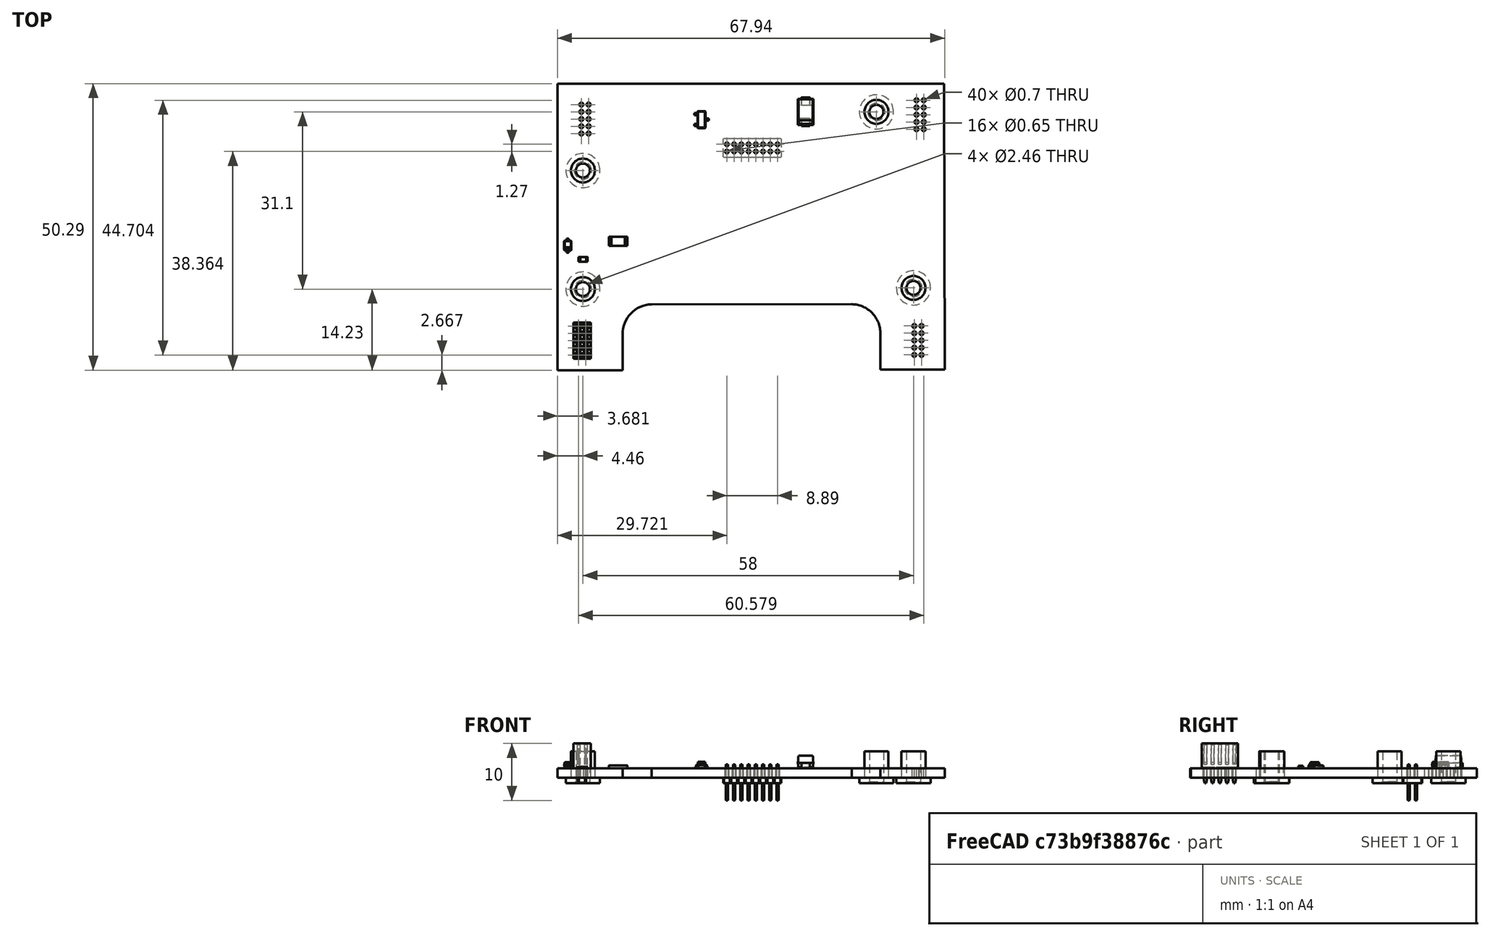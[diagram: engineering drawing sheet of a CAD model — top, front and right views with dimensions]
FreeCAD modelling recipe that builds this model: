
FCSTD DOCUMENT  (FreeCAD 1.0R39109 (Git))
Label: DICAddonBoard
License: All rights reserved
LicenseURL: http://en.wikipedia.org/wiki/All_rights_reserved
objects: App::Link×70, Part::Feature×18, App::Part×5, PartDesign::CoordinateSystem×1, Sketcher::SketchObject×1
note: 21 computed .brp shape members not serialized (recipe doc carries the construction recipe); baked Part::Feature solids carry a one-line shape summary decoded from their .brp

FEATURE [PartDesign::CoordinateSystem] Local_CS_25db
  AttacherType = Attacher::AttachEngine3D
  MapMode = 2
FEATURE [Part::Feature] Pcb_25db
  shape: bbox 67.95 x 50.29 x 1.6 mm, 68 faces (baked)
FEATURE [Sketcher::SketchObject] PCB_Sketch_25db
  ArcFitTolerance = 1e-06
  FullyConstrained = false
  MakeInternals = false
  sketch-geometry (10):
    g0: LineSegment StartX=11.938 StartY=-11.938 StartZ=0 EndX=11.938 EndY=-62.23 EndZ=0
    g1: LineSegment StartX=68.58 StartY=-62.103 StartZ=0 EndX=79.883 EndY=-62.103 EndZ=0
    g2: LineSegment StartX=11.938 StartY=-62.23 StartZ=0 EndX=23.3806 EndY=-62.23 EndZ=0
    g3: LineSegment StartX=23.3806 StartY=-62.23 StartZ=0 EndX=23.368 EndY=-55.9897 EndZ=0
    g4: LineSegment StartX=79.756 StartY=-11.938 StartZ=0 EndX=11.938 EndY=-11.938 EndZ=0
    g5: LineSegment StartX=68.5926 StartY=-55.8627 StartZ=0 EndX=68.58 EndY=-62.103 EndZ=0
    g6: LineSegment StartX=28.448 StartY=-50.673 StartZ=0 EndX=63.5588 EndY=-50.6595 EndZ=0
    g7: LineSegment StartX=79.883 StartY=-62.103 StartZ=0 EndX=79.756 EndY=-11.938 EndZ=0
    g8: ArcOfCircle CenterX=28.5729 CenterY=-55.8776 CenterZ=0 NormalX=0 NormalY=0 NormalZ=-1 AngleXU=-0.0215457 Radius=5.20607 StartAngle=0 EndAngle=1.56835
    g9: ArcOfCircle CenterX=63.5 CenterY=-55.753 CenterZ=0 NormalX=0 NormalY=0 NormalZ=-1 AngleXU=1.58235 Radius=5.09379 StartAngle=-4.7832e-11 EndAngle=1.58079
  constraints (10):
    c: Coincident(g0,g2)
    c: Coincident(g0,g4)
    c: Coincident(g3,g8)
    c: Coincident(g2,g3)
    c: Coincident(g6,g8)
    c: Coincident(g6,g9)
    c: Coincident(g1,g5)
    c: Coincident(g5,g9)
    c: Coincident(g4,g7)
    c: Coincident(g1,g7)
FEATURE [Part::Feature] Shape  label="Q6_SOT_23_ffd5320711a5"
  Placement = pos=(37.211,-18.262,0) rot=(0,0,1;0rad)
  shape: bbox 2.5 x 3 x 1.2 mm, 76 faces (baked)
FEATURE [Part::Feature] Shape001  label="D16_D_SOD_323_d7651d96f6c3"
  Placement = pos=(13.7425,-40.366,0) rot=(0,0,1;1.5708rad)
  shape: bbox 1.25 x 2.5 x 1.1 mm, 67 faces (baked)
FEATURE [Part::Feature] Shape002  label="J6_PinSocket_2x05_P127mm_Vertical_83ee9fbb584e"
  Placement = pos=(16.891,-54.483,0) rot=(0,0,1;0rad)
  shape: bbox 3.05 x 6.35 x 7 mm, 320 faces (baked)
FEATURE [Part::Feature] Shape003  label="R41_R_0603_1608Metric_127fa2614279"
  Placement = pos=(16.433,-42.799,0) rot=(0,0,1;0rad)
  shape: bbox 1.6 x 0.8 x 0.45 mm, 26 faces (baked)
FEATURE [App::Link] R41_R_0603_1608Metric_127fa2614279_ln_  label="R12_R_0603_1608Metric_a0e0216bc4ce"
  LinkPlacement = pos=(29.9212,-15.0876,0) rot=(0,0,1;3.14159rad)
  LinkedObject = -> Shape003
  Placement = pos=(29.9212,-15.0876,0) rot=(0,0,1;3.14159rad)
FEATURE [App::Link] R41_R_0603_1608Metric_127fa2614279_ln_001  label="R13_R_0603_1608Metric_473b31106c1b"
  LinkPlacement = pos=(32.639,-18.77,0) rot=(0,0,1;1.5708rad)
  LinkedObject = -> Shape003
  Placement = pos=(32.639,-18.77,0) rot=(0,0,1;1.5708rad)
FEATURE [Part::Feature] Shape004  label="D6_D_SMA_735d77270f2b"
  Placement = pos=(55.477,-16.896,0) rot=(0,0,1;1.5708rad)
  shape: bbox 2.7 x 5 x 2.22 mm, 41 faces (baked)
FEATURE [App::Link] R41_R_0603_1608Metric_127fa2614279_ln_002  label="R9_R_0603_1608Metric_79f8a3dd54a6"
  LinkPlacement = pos=(61.214,-13.9059,0) rot=(0,0,1;3.14159rad)
  LinkedObject = -> Shape003
  Placement = pos=(61.214,-13.9059,0) rot=(0,0,1;3.14159rad)
FEATURE [App::Link] R41_R_0603_1608Metric_127fa2614279_ln_003  label="R31_R_0603_1608Metric_c49473b8d088"
  LinkPlacement = pos=(50.473,-46.8085,0) rot=(0,0,1;1.5708rad)
  LinkedObject = -> Shape003
  Placement = pos=(50.473,-46.8085,0) rot=(0,0,1;1.5708rad)
FEATURE [App::Link] R41_R_0603_1608Metric_127fa2614279_ln_004  label="R14_R_0603_1608Metric_d7197a96d642"
  LinkPlacement = pos=(37.41,-15.722,0) rot=(0,0,1;0rad)
  LinkedObject = -> Shape003
  Placement = pos=(37.41,-15.722,0) rot=(0,0,1;0rad)
FEATURE [App::Link] R41_R_0603_1608Metric_127fa2614279_ln_005  label="R35_R_0603_1608Metric_1226fcb64f1c"
  LinkPlacement = pos=(47.933,-37.9245,0) rot=(0,0,1;0rad)
  LinkedObject = -> Shape003
  Placement = pos=(47.933,-37.9245,0) rot=(0,0,1;0rad)
FEATURE [App::Link] D6_D_SMA_735d77270f2b_ln_  label="D17_D_SMA_0876cbf78d6f"
  LinkPlacement = pos=(20.828,-34.925,0) rot=(0,0,1;1.5708rad)
  LinkedObject = -> Shape004
  Placement = pos=(20.828,-34.925,0) rot=(0,0,1;1.5708rad)
FEATURE [App::Link] D6_D_SMA_735d77270f2b_ln_001  label="D15_D_SMA_1207fe425828"
  LinkPlacement = pos=(53.255,-43.21,0) rot=(0,0,1;0rad)
  LinkedObject = -> Shape004
  Placement = pos=(53.255,-43.21,0) rot=(0,0,1;0rad)
FEATURE [App::Link] D16_D_SOD_323_d7651d96f6c3_ln_  label="D13_D_SOD_323_07ad6b2cef4e"
  LinkPlacement = pos=(47.826,-32.3365,0) rot=(0,0,1;3.14159rad)
  LinkedObject = -> Shape001
  Placement = pos=(47.826,-32.3365,0) rot=(0,0,1;3.14159rad)
FEATURE [App::Link] R41_R_0603_1608Metric_127fa2614279_ln_006  label="R32_R_0603_1608Metric_48fbb2cf6ecc"
  LinkPlacement = pos=(56.061,-46.705,0) rot=(0,0,1;1.5708rad)
  LinkedObject = -> Shape003
  Placement = pos=(56.061,-46.705,0) rot=(0,0,1;1.5708rad)
FEATURE [App::Link] R41_R_0603_1608Metric_127fa2614279_ln_007  label="R24_R_0603_1608Metric_9565dda51c7b"
  LinkPlacement = pos=(50.461,-36.098,0) rot=(0,0,1;1.5708rad)
  LinkedObject = -> Shape003
  Placement = pos=(50.461,-36.098,0) rot=(0,0,1;1.5708rad)
FEATURE [App::Link] R41_R_0603_1608Metric_127fa2614279_ln_008  label="R39_R_0603_1608Metric_0d8059b3905e"
  LinkPlacement = pos=(27.857,-32.131,0) rot=(0,0,1;3.14159rad)
  LinkedObject = -> Shape003
  Placement = pos=(27.857,-32.131,0) rot=(0,0,1;3.14159rad)
FEATURE [App::Link] R41_R_0603_1608Metric_127fa2614279_ln_009  label="R11_R_0603_1608Metric_e8feb780e285"
  LinkPlacement = pos=(37.363,-14.198,0) rot=(0,0,1;0rad)
  LinkedObject = -> Shape003
  Placement = pos=(37.363,-14.198,0) rot=(0,0,1;0rad)
FEATURE [App::Link] D6_D_SMA_735d77270f2b_ln_002  label="D9_D_SMA_59bcf57c5f9f"
  LinkPlacement = pos=(51.943,-16.865,0) rot=(0,0,1;1.5708rad)
  LinkedObject = -> Shape004
  Placement = pos=(51.943,-16.865,0) rot=(0,0,1;1.5708rad)
FEATURE [App::Link] D6_D_SMA_735d77270f2b_ln_003  label="D18_D_SMA_56b2f2076145"
  LinkPlacement = pos=(24.362,-34.925,0) rot=(0,0,1;1.5708rad)
  LinkedObject = -> Shape004
  Placement = pos=(24.362,-34.925,0) rot=(0,0,1;1.5708rad)
FEATURE [App::Link] R41_R_0603_1608Metric_127fa2614279_ln_010  label="R37_R_0603_1608Metric_b9a5ae661070"
  LinkPlacement = pos=(17.25,-32.004,0) rot=(0,0,1;0rad)
  LinkedObject = -> Shape003
  Placement = pos=(17.25,-32.004,0) rot=(0,0,1;0rad)
FEATURE [App::Link] R41_R_0603_1608Metric_127fa2614279_ln_011  label="R34_R_0603_1608Metric_5b0c20e38f9c"
  LinkPlacement = pos=(44.504,-34.1145,0) rot=(0,0,1;3.14159rad)
  LinkedObject = -> Shape003
  Placement = pos=(44.504,-34.1145,0) rot=(0,0,1;3.14159rad)
FEATURE [App::Link] R41_R_0603_1608Metric_127fa2614279_ln_012  label="R33_R_0603_1608Metric_6760e7cc6251"
  LinkPlacement = pos=(44.0995,-32.3365,0) rot=(0,0,1;3.14159rad)
  LinkedObject = -> Shape003
  Placement = pos=(44.0995,-32.3365,0) rot=(0,0,1;3.14159rad)
FEATURE [App::Link] D16_D_SOD_323_d7651d96f6c3_ln_001  label="D4_D_SOD_323_fbe22daa305a"
  LinkPlacement = pos=(30.861,-18.2655,0) rot=(0,0,1;1.5708rad)
  LinkedObject = -> Shape001
  Placement = pos=(30.861,-18.2655,0) rot=(0,0,1;1.5708rad)
FEATURE [Part::Feature] Shape005  label="TH6_R_1206_3216Metric_a4174fc2a386"
  Placement = pos=(22.584,-39.624,0) rot=(0,0,1;3.14159rad)
  shape: bbox 3.2 x 1.6 x 0.55 mm, 26 faces (baked)
FEATURE [App::Link] R41_R_0603_1608Metric_127fa2614279_ln_013  label="R40_R_0603_1608Metric_99d0bb74b373"
  LinkPlacement = pos=(13.7425,-36.703,0) rot=(0,0,1;1.5708rad)
  LinkedObject = -> Shape003
  Placement = pos=(13.7425,-36.703,0) rot=(0,0,1;1.5708rad)
FEATURE [App::Link] R41_R_0603_1608Metric_127fa2614279_ln_014  label="R8_R_0603_1608Metric_f9849ceb0926"
  LinkPlacement = pos=(61.087,-19.4939,0) rot=(0,0,1;3.14159rad)
  LinkedObject = -> Shape003
  Placement = pos=(61.087,-19.4939,0) rot=(0,0,1;3.14159rad)
FEATURE [App::Link] R41_R_0603_1608Metric_127fa2614279_ln_015  label="R36_R_0603_1608Metric_b33a5e9c3cf1"
  LinkPlacement = pos=(17.377,-37.592,0) rot=(0,0,1;3.14159rad)
  LinkedObject = -> Shape003
  Placement = pos=(17.377,-37.592,0) rot=(0,0,1;3.14159rad)
FEATURE [App::Link] Q6_SOT_23_ffd5320711a5_ln_  label="Q18_SOT_23_5dae6c215293"
  LinkPlacement = pos=(16.6635,-40.259,0) rot=(0,0,1;3.14159rad)
  LinkedObject = -> Shape
  Placement = pos=(16.6635,-40.259,0) rot=(0,0,1;3.14159rad)
FEATURE [App::Link] J6_PinSocket_2x05_P127mm_Vertical_83ee9fbb584e_ln_  label="J2_PinSocket_2x05_P127mm_Vertical_fade8c78a2a7"
  LinkPlacement = pos=(76.2,-14.859,0) rot=(0,0,1;0rad)
  LinkedObject = -> Shape002
  Placement = pos=(76.2,-14.859,0) rot=(0,0,1;0rad)
FEATURE [App::Link] J6_PinSocket_2x05_P127mm_Vertical_83ee9fbb584e_ln_001  label="J5_PinSocket_2x05_P127mm_Vertical_c59673f5576a"
  LinkPlacement = pos=(16.129,-20.701,0) rot=(0,0,1;3.14159rad)
  LinkedObject = -> Shape002
  Placement = pos=(16.129,-20.701,0) rot=(0,0,1;3.14159rad)
FEATURE [App::Link] TH6_R_1206_3216Metric_a4174fc2a386_ln_  label="TH2_R_1206_3216Metric_52bc38417804"
  LinkPlacement = pos=(41.529,-18.262,0) rot=(0,0,1;1.5708rad)
  LinkedObject = -> Shape005
  Placement = pos=(41.529,-18.262,0) rot=(0,0,1;1.5708rad)
FEATURE [App::Link] D6_D_SMA_735d77270f2b_ln_004  label="D14_D_SMA_40db2f55f09c"
  LinkPlacement = pos=(53.255,-39.584,0) rot=(0,0,1;0rad)
  LinkedObject = -> Shape004
  Placement = pos=(53.255,-39.584,0) rot=(0,0,1;0rad)
FEATURE [App::Link] R41_R_0603_1608Metric_127fa2614279_ln_016  label="R42_R_0603_1608Metric_3962cb7ffa21"
  LinkPlacement = pos=(19.3305,-40.386,0) rot=(0,0,1;1.5708rad)
  LinkedObject = -> Shape003
  Placement = pos=(19.3305,-40.386,0) rot=(0,0,1;1.5708rad)
FEATURE [App::Link] J6_PinSocket_2x05_P127mm_Vertical_83ee9fbb584e_ln_002  label="J4_PinSocket_2x05_P127mm_Vertical_839abc38b667"
  LinkPlacement = pos=(75.819,-54.473,0) rot=(0,0,1;0rad)
  LinkedObject = -> Shape002
  Placement = pos=(75.819,-54.473,0) rot=(0,0,1;0rad)
FEATURE [App::Link] R41_R_0603_1608Metric_127fa2614279_ln_017  label="R10_R_0603_1608Metric_f7e09fcf0586"
  LinkPlacement = pos=(48.387,-13.563,0) rot=(0,0,1;3.14159rad)
  LinkedObject = -> Shape003
  Placement = pos=(48.387,-13.563,0) rot=(0,0,1;3.14159rad)
FEATURE [App::Link] R41_R_0603_1608Metric_127fa2614279_ln_018  label="R38_R_0603_1608Metric_5053fa264887"
  LinkPlacement = pos=(27.984,-37.719,0) rot=(0,0,1;3.14159rad)
  LinkedObject = -> Shape003
  Placement = pos=(27.984,-37.719,0) rot=(0,0,1;3.14159rad)
FEATURE [App::Link] R41_R_0603_1608Metric_127fa2614279_ln_019  label="R30_R_0603_1608Metric_0ef8a02bf31b"
  LinkPlacement = pos=(56.061,-36.0085,0) rot=(0,0,-1;1.5708rad)
  LinkedObject = -> Shape003
  Placement = pos=(56.061,-36.0085,0) rot=(0,0,-1;1.5708rad)
FEATURE [App::Link] Q6_SOT_23_ffd5320711a5_ln_001  label="Q15_SOT_23_f88ca606a138"
  LinkPlacement = pos=(47.933,-35.2575,0) rot=(0,0,1;1.5708rad)
  LinkedObject = -> Shape
  Placement = pos=(47.933,-35.2575,0) rot=(0,0,1;1.5708rad)
FEATURE [App::Link] TH6_R_1206_3216Metric_a4174fc2a386_ln_001  label="TH4_R_1206_3216Metric_6cedd577e318"
  LinkPlacement = pos=(48.568,-41.178,0) rot=(0,0,1;1.5708rad)
  LinkedObject = -> Shape005
  Placement = pos=(48.568,-41.178,0) rot=(0,0,1;1.5708rad)
FEATURE [App::Part] Top_25db
  Group = -> [Shape,Shape001,Shape002,Shape003,R41_R_0603_1608Metric_127fa2614279_ln_,R41_R_0603_1608Metric_127fa2614279_ln_001,Shape004,R41_R_0603_1608Metric_127fa2614279_ln_002,R41_R_0603_1608Metric_127fa2614279_ln_003,R41_R_0603_1608Metric_127fa2614279_ln_004,R41_R_0603_1608Metric_127fa2614279_ln_005,D6_D_SMA_735d77270f2b_ln_,D6_D_SMA_735d77270f2b_ln_001,D16_D_SOD_323_d7651d96f6c3_ln_,+26 more]
  Origin = -> Origin003
FEATURE [App::Link] R41_R_0603_1608Metric_127fa2614279_ln_020  label="R16_R_0603_1608Metric_7932c1e08af1"
  LinkPlacement = pos=(41.275,-42.313,-1.6) rot=(0.707107,0.707107,0;3.14159rad)
  LinkedObject = -> Shape003
  Placement = pos=(41.275,-42.313,-1.6) rot=(0.707107,0.707107,0;3.14159rad)
FEATURE [App::Link] R41_R_0603_1608Metric_127fa2614279_ln_021  label="R25_R_0603_1608Metric_af43064dc6b6"
  LinkPlacement = pos=(74.996,-34.8215,-1.6) rot=(0.707107,-0.707107,0;3.14159rad)
  LinkedObject = -> Shape003
  Placement = pos=(74.996,-34.8215,-1.6) rot=(0.707107,-0.707107,0;3.14159rad)
FEATURE [App::Link] R41_R_0603_1608Metric_127fa2614279_ln_022  label="R3_R_0603_1608Metric_90eb9fac611c"
  LinkPlacement = pos=(27.8525,-37.777,-1.6) rot=(0.707107,0.707107,0;3.14159rad)
  LinkedObject = -> Shape003
  Placement = pos=(27.8525,-37.777,-1.6) rot=(0.707107,0.707107,0;3.14159rad)
FEATURE [App::Link] R41_R_0603_1608Metric_127fa2614279_ln_023  label="R2_R_0603_1608Metric_a95339afed33"
  LinkPlacement = pos=(22.3534,-27.095,-1.6) rot=(0.707107,0.707107,0;3.14159rad)
  LinkedObject = -> Shape003
  Placement = pos=(22.3534,-27.095,-1.6) rot=(0.707107,0.707107,0;3.14159rad)
FEATURE [App::Link] R41_R_0603_1608Metric_127fa2614279_ln_024  label="R29_R_0603_1608Metric_a323e5d2541c"
  LinkPlacement = pos=(69.088,-31.2255,-1.6) rot=(0.707107,-0.707107,0;3.14159rad)
  LinkedObject = -> Shape003
  Placement = pos=(69.088,-31.2255,-1.6) rot=(0.707107,-0.707107,0;3.14159rad)
FEATURE [App::Link] R41_R_0603_1608Metric_127fa2614279_ln_025  label="R1_R_0603_1608Metric_b07fb1c3085f"
  LinkPlacement = pos=(27.9414,-27.222,-1.6) rot=(0.707107,0.707107,0;3.14159rad)
  LinkedObject = -> Shape003
  Placement = pos=(27.9414,-27.222,-1.6) rot=(0.707107,0.707107,0;3.14159rad)
FEATURE [App::Link] R41_R_0603_1608Metric_127fa2614279_ln_026  label="R18_R_0603_1608Metric_5d82281689e8"
  LinkPlacement = pos=(26.7885,-42.672,-1.6) rot=(0,1,0;3.14159rad)
  LinkedObject = -> Shape003
  Placement = pos=(26.7885,-42.672,-1.6) rot=(0,1,0;3.14159rad)
FEATURE [App::Link] R41_R_0603_1608Metric_127fa2614279_ln_027  label="R27_R_0603_1608Metric_214af474eae8"
  LinkPlacement = pos=(75.9085,-41.275,-1.6) rot=(1,0,0;3.14159rad)
  LinkedObject = -> Shape003
  Placement = pos=(75.9085,-41.275,-1.6) rot=(1,0,0;3.14159rad)
FEATURE [App::Link] D6_D_SMA_735d77270f2b_ln_005  label="D11_D_SMA_1ba17688d2f4"
  LinkPlacement = pos=(38.449,-38.735,-1.6) rot=(1,0,0;3.14159rad)
  LinkedObject = -> Shape004
  Placement = pos=(38.449,-38.735,-1.6) rot=(1,0,0;3.14159rad)
FEATURE [App::Link] R41_R_0603_1608Metric_127fa2614279_ln_028  label="R17_R_0603_1608Metric_89ce4ec7833c"
  LinkPlacement = pos=(26.8355,-48.26,-1.6) rot=(1,0,0;3.14159rad)
  LinkedObject = -> Shape003
  Placement = pos=(26.8355,-48.26,-1.6) rot=(1,0,0;3.14159rad)
FEATURE [App::Link] R41_R_0603_1608Metric_127fa2614279_ln_029  label="R6_R_0603_1608Metric_1afd86b5277d"
  LinkPlacement = pos=(35.7265,-28.421,-1.6) rot=(0.707107,0.707107,0;3.14159rad)
  LinkedObject = -> Shape003
  Placement = pos=(35.7265,-28.421,-1.6) rot=(0.707107,0.707107,0;3.14159rad)
FEATURE [App::Link] D16_D_SOD_323_d7651d96f6c3_ln_002  label="D10_D_SOD_323_00e277693b72"
  LinkPlacement = pos=(33.167,-46.0745,-1.6) rot=(0,1,0;3.14159rad)
  LinkedObject = -> Shape001
  Placement = pos=(33.167,-46.0745,-1.6) rot=(0,1,0;3.14159rad)
FEATURE [Part::Feature] Shape006  label="J3_PinHeader_2x08_P127mm_Vertical_13ff719d442c"
  Placement = pos=(50.551,-23.866,-1.6) rot=(0.707107,0.707107,0;3.14159rad)
  shape: bbox 10.16 x 3.4 x 6.3 mm, 340 faces (baked)
FEATURE [App::Link] D6_D_SMA_735d77270f2b_ln_006  label="D3_D_SMA_cd35c1e422c8"
  LinkPlacement = pos=(25.0905,-34.268,-1.6) rot=(0,1,0;3.14159rad)
  LinkedObject = -> Shape004
  Placement = pos=(25.0905,-34.268,-1.6) rot=(0,1,0;3.14159rad)
FEATURE [App::Link] R41_R_0603_1608Metric_127fa2614279_ln_030  label="R7_R_0603_1608Metric_afc0888e760f"
  LinkPlacement = pos=(30.6465,-28.172,-1.6) rot=(0.707107,-0.707107,0;3.14159rad)
  LinkedObject = -> Shape003
  Placement = pos=(30.6465,-28.172,-1.6) rot=(0.707107,-0.707107,0;3.14159rad)
FEATURE [App::Link] R41_R_0603_1608Metric_127fa2614279_ln_031  label="R28_R_0603_1608Metric_a4707fec901c"
  LinkPlacement = pos=(61.595,-31.0515,-1.6) rot=(0.707107,0.707107,0;3.14159rad)
  LinkedObject = -> Shape003
  Placement = pos=(61.595,-31.0515,-1.6) rot=(0.707107,0.707107,0;3.14159rad)
FEATURE [App::Link] D16_D_SOD_323_d7651d96f6c3_ln_003  label="D5_D_SOD_323_8140ef0d37c0"
  LinkPlacement = pos=(63.373,-31.095,-1.6) rot=(0.707107,0.707107,0;3.14159rad)
  LinkedObject = -> Shape001
  Placement = pos=(63.373,-31.095,-1.6) rot=(0.707107,0.707107,0;3.14159rad)
FEATURE [App::Link] D16_D_SOD_323_d7651d96f6c3_ln_004  label="D1_D_SOD_323_d5d77308ac17"
  LinkPlacement = pos=(33.1665,-31.347,-1.6) rot=(1,0,0;3.14159rad)
  LinkedObject = -> Shape001
  Placement = pos=(33.1665,-31.347,-1.6) rot=(1,0,0;3.14159rad)
FEATURE [App::Link] Q6_SOT_23_ffd5320711a5_ln_002  label="Q10_SOT_23_8cad5c28a702"
  LinkPlacement = pos=(33.147,-43.0265,-1.6) rot=(0.707107,-0.707107,0;3.14159rad)
  LinkedObject = -> Shape
  Placement = pos=(33.147,-43.0265,-1.6) rot=(0.707107,-0.707107,0;3.14159rad)
FEATURE [App::Link] R41_R_0603_1608Metric_127fa2614279_ln_032  label="R23_R_0603_1608Metric_7848ec0b3468"
  LinkPlacement = pos=(65.151,-41.529,-1.6) rot=(1,0,0;3.14159rad)
  LinkedObject = -> Shape003
  Placement = pos=(65.151,-41.529,-1.6) rot=(1,0,0;3.14159rad)
FEATURE [App::Link] TH6_R_1206_3216Metric_a4174fc2a386_ln_002  label="TH5_R_1206_3216Metric_65273da20f15"
  LinkPlacement = pos=(70.612,-34.036,-1.6) rot=(0,1,0;3.14159rad)
  LinkedObject = -> Shape005
  Placement = pos=(70.612,-34.036,-1.6) rot=(0,1,0;3.14159rad)
FEATURE [App::Link] R41_R_0603_1608Metric_127fa2614279_ln_033  label="R19_R_0603_1608Metric_b451ed5a0d5d"
  LinkPlacement = pos=(29.845,-41.021,-1.6) rot=(0.707107,-0.707107,0;3.14159rad)
  LinkedObject = -> Shape003
  Placement = pos=(29.845,-41.021,-1.6) rot=(0.707107,-0.707107,0;3.14159rad)
FEATURE [App::Link] R41_R_0603_1608Metric_127fa2614279_ln_034  label="R21_R_0603_1608Metric_086685fbb64e"
  LinkPlacement = pos=(64.262,-35.0285,-1.6) rot=(0.707107,0.707107,0;3.14159rad)
  LinkedObject = -> Shape003
  Placement = pos=(64.262,-35.0285,-1.6) rot=(0.707107,0.707107,0;3.14159rad)
FEATURE [App::Link] R41_R_0603_1608Metric_127fa2614279_ln_035  label="R20_R_0603_1608Metric_74876393d18b"
  LinkPlacement = pos=(37.211,-46.0745,-1.6) rot=(1,0,0;3.14159rad)
  LinkedObject = -> Shape003
  Placement = pos=(37.211,-46.0745,-1.6) rot=(1,0,0;3.14159rad)
FEATURE [App::Link] R41_R_0603_1608Metric_127fa2614279_ln_036  label="R15_R_0603_1608Metric_62f7b17bc8fc"
  LinkPlacement = pos=(35.687,-42.313,-1.6) rot=(0.707107,-0.707107,0;3.14159rad)
  LinkedObject = -> Shape003
  Placement = pos=(35.687,-42.313,-1.6) rot=(0.707107,-0.707107,0;3.14159rad)
FEATURE [App::Link] D6_D_SMA_735d77270f2b_ln_007  label="D2_D_SMA_e8f0f4ea1691"
  LinkPlacement = pos=(25.0905,-30.734,-1.6) rot=(0,1,0;3.14159rad)
  LinkedObject = -> Shape004
  Placement = pos=(25.0905,-30.734,-1.6) rot=(0,1,0;3.14159rad)
FEATURE [App::Link] TH6_R_1206_3216Metric_a4174fc2a386_ln_003  label="TH1_R_1206_3216Metric_ce9414de59a2"
  LinkPlacement = pos=(29.8845,-32.617,-1.6) rot=(0.707107,0.707107,0;3.14159rad)
  LinkedObject = -> Shape005
  Placement = pos=(29.8845,-32.617,-1.6) rot=(0.707107,0.707107,0;3.14159rad)
FEATURE [App::Link] D6_D_SMA_735d77270f2b_ln_008  label="D12_D_SMA_21d0ff51f2b2"
  LinkPlacement = pos=(38.449,-35.201,-1.6) rot=(1,0,0;3.14159rad)
  LinkedObject = -> Shape004
  Placement = pos=(38.449,-35.201,-1.6) rot=(1,0,0;3.14159rad)
FEATURE [App::Link] TH6_R_1206_3216Metric_a4174fc2a386_ln_004  label="TH3_R_1206_3216Metric_be97d367e00d"
  LinkPlacement = pos=(33.782,-36.852,-1.6) rot=(0.707107,-0.707107,0;3.14159rad)
  LinkedObject = -> Shape005
  Placement = pos=(33.782,-36.852,-1.6) rot=(0.707107,-0.707107,0;3.14159rad)
FEATURE [App::Link] D6_D_SMA_735d77270f2b_ln_009  label="D8_D_SMA_7218f854b2e2"
  LinkPlacement = pos=(72.39,-38.703,-1.6) rot=(0.707107,-0.707107,0;3.14159rad)
  LinkedObject = -> Shape004
  Placement = pos=(72.39,-38.703,-1.6) rot=(0.707107,-0.707107,0;3.14159rad)
FEATURE [App::Link] Q6_SOT_23_ffd5320711a5_ln_003  label="Q3_SOT_23_dc7f19c19d1b"
  LinkPlacement = pos=(33.1865,-28.299,-1.6) rot=(0.707107,-0.707107,0;3.14159rad)
  LinkedObject = -> Shape
  Placement = pos=(33.1865,-28.299,-1.6) rot=(0.707107,-0.707107,0;3.14159rad)
FEATURE [App::Link] R41_R_0603_1608Metric_127fa2614279_ln_037  label="R4_R_0603_1608Metric_2e89caf32d98"
  LinkPlacement = pos=(22.2645,-37.8005,-1.6) rot=(0.707107,-0.707107,0;3.14159rad)
  LinkedObject = -> Shape003
  Placement = pos=(22.2645,-37.8005,-1.6) rot=(0.707107,-0.707107,0;3.14159rad)
FEATURE [App::Link] R41_R_0603_1608Metric_127fa2614279_ln_038  label="R22_R_0603_1608Metric_94414fea2e43"
  LinkPlacement = pos=(33.1235,-40.3595,-1.6) rot=(1,0,0;3.14159rad)
  LinkedObject = -> Shape003
  Placement = pos=(33.1235,-40.3595,-1.6) rot=(1,0,0;3.14159rad)
FEATURE [App::Link] D6_D_SMA_735d77270f2b_ln_010  label="D7_D_SMA_2e44e889cb4e"
  LinkPlacement = pos=(68.834,-38.703,-1.6) rot=(0.707107,-0.707107,0;3.14159rad)
  LinkedObject = -> Shape004
  Placement = pos=(68.834,-38.703,-1.6) rot=(0.707107,-0.707107,0;3.14159rad)
FEATURE [App::Link] R41_R_0603_1608Metric_127fa2614279_ln_039  label="R26_R_0603_1608Metric_d41138b5fa4f"
  LinkPlacement = pos=(64.389,-28.281,-1.6) rot=(1,0,0;3.14159rad)
  LinkedObject = -> Shape003
  Placement = pos=(64.389,-28.281,-1.6) rot=(1,0,0;3.14159rad)
FEATURE [App::Link] Q6_SOT_23_ffd5320711a5_ln_004  label="Q12_SOT_23_6e3906f2bc9c"
  LinkPlacement = pos=(66.421,-31.202,-1.6) rot=(0,1,0;3.14159rad)
  LinkedObject = -> Shape
  Placement = pos=(66.421,-31.202,-1.6) rot=(0,1,0;3.14159rad)
FEATURE [App::Link] R41_R_0603_1608Metric_127fa2614279_ln_040  label="R5_R_0603_1608Metric_a69d22cc4bcb"
  LinkPlacement = pos=(37.719,-30.353,-1.6) rot=(0.707107,0.707107,0;3.14159rad)
  LinkedObject = -> Shape003
  Placement = pos=(37.719,-30.353,-1.6) rot=(0.707107,0.707107,0;3.14159rad)
FEATURE [App::Part] Bot_25db
  Group = -> [R41_R_0603_1608Metric_127fa2614279_ln_020,R41_R_0603_1608Metric_127fa2614279_ln_021,R41_R_0603_1608Metric_127fa2614279_ln_022,R41_R_0603_1608Metric_127fa2614279_ln_023,R41_R_0603_1608Metric_127fa2614279_ln_024,R41_R_0603_1608Metric_127fa2614279_ln_025,R41_R_0603_1608Metric_127fa2614279_ln_026,R41_R_0603_1608Metric_127fa2614279_ln_027,D6_D_SMA_735d77270f2b_ln_005,+28 more]
  Origin = -> Origin004
FEATURE [App::Part] Step_Models_25db
  Group = -> [Top_25db,Bot_25db]
  Origin = -> Origin002
FEATURE [Part::Feature] pads_area001  label="topPads_25db"
  Placement = pos=(0,0,0.02) rot=(0,0,1;0rad)
  shape: bbox 65.44 x 47.07 x 2e-07 mm, 247 faces, 0 solids (baked)
FEATURE [Part::Feature] Shape008  label="topTracks_25db"
  Placement = pos=(0,0,0.01) rot=(0,0,1;0rad)
  shape: bbox 65.02 x 45.59 x 2e-07 mm, 81 faces, 0 solids (baked)
FEATURE [Part::Feature] pads_area003  label="botPads_25db"
  Placement = pos=(0,0,-1.62) rot=(0,0,1;0rad)
  shape: bbox 65.44 x 47.03 x 2e-07 mm, 248 faces, 0 solids (baked)
FEATURE [Part::Feature] Shape010  label="botTracks_25db"
  Placement = pos=(0,0,-1.61) rot=(0,0,1;0rad)
  shape: bbox 65.32 x 46.99 x 2e-07 mm, 80 faces, 0 solids (baked)
FEATURE [Part::Feature] botSilks_c76e
  Placement = pos=(0,0,-1.67) rot=(0,0,1;0rad)
  shape: bbox 83.53 x 49.14 x 2e-07 mm, 230 faces, 0 solids (baked)
FEATURE [Part::Feature] topSilks_caba
  Placement = pos=(0,0,0.07) rot=(0,0,1;0rad)
  shape: bbox 64.67 x 49.71 x 2e-07 mm, 286 faces, 0 solids (baked)
FEATURE [Part::Feature] Part__Feature  label="1"
  Placement = pos=(16.4,-27.2,-1.6) rot=(0,1,0;3.14159rad)
  shape: bbox 6 x 6 x 5.6 mm, 7 faces (baked)
FEATURE [Part::Feature] Part__Feature001  label="1001"
  Placement = pos=(67.9,-16.9,-1.6) rot=(0,1,0;3.14159rad)
  shape: bbox 6 x 6 x 5.6 mm, 7 faces (baked)
FEATURE [Part::Feature] Part__Feature002  label="1002"
  Placement = pos=(16.4,-48,-1.6) rot=(0,1,0;3.14159rad)
  shape: bbox 6 x 6 x 5.6 mm, 7 faces (baked)
FEATURE [Part::Feature] Part__Feature003  label="1003"
  Placement = pos=(74.4,-47.8,-1.6) rot=(0,1,0;3.14159rad)
  shape: bbox 6 x 6 x 5.6 mm, 7 faces (baked)
FEATURE [App::Part] Board_Geoms_25db
  Group = -> [Pcb_25db,PCB_Sketch_25db,pads_area001,Shape008,pads_area003,Shape010,botSilks_c76e,topSilks_caba,Part__Feature,Part__Feature001,Part__Feature002,Part__Feature003]
  Origin = -> Origin
FEATURE [App::Part] Board_25db  label="DIC_Addon"
  Group = -> [Local_CS_25db,Board_Geoms_25db,Step_Models_25db]
  Origin = -> Origin001
